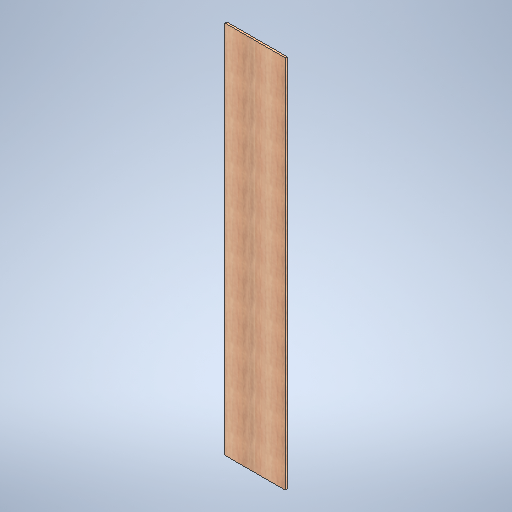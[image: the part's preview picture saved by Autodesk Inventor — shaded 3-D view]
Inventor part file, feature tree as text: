
AUTODESK INVENTOR PART (.ipt)
format: ipt  version: 2025.1 (Build 291241020, 241B)  size: 330,752 bytes
history: native  units: in
note: dims shown in document units (in); Inventor stores cm internally (conversion verified against a paired STEP export)
features: extrude x1, sketch x1
ambient origin geometry x8: Origin, YZ Plane, XZ Plane, XY Plane, X Axis, Y Axis, Z Axis, Center Point
bodies: Solid1 (feature_tree)
feature tree (2):
  extrude  "Extrusion1"  Depth=15.459in
  sketch  "Sketch1"  dims[d2=96.0in d3=15.459in d4=0.5in d5=0.0in]
